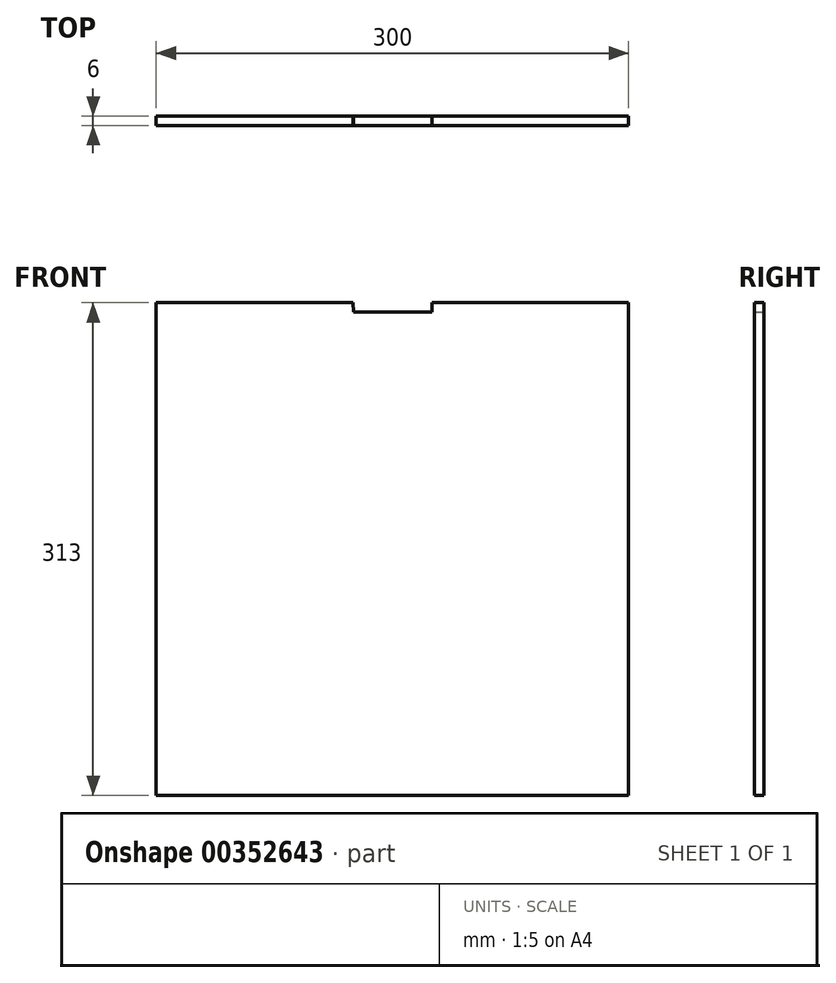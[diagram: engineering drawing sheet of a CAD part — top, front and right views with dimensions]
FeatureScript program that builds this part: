
annotation { "Feature Type Name" : "Feature", "Feature Type Description" : "" }
export const myFeature = defineFeature(function(context is Context, id is Id, definition is map)
    precondition{}
    {
        {
            var Q0;
            Q0=qCreatedBy(makeId("Front.planeOp"),FACE);
            var sketch = newSketch(context, id + "F0", { "sketchPlane" : qUnion([Q0])});
            skLineSegment(sketch, "E0", {"start": v(-46.12, 181.72) * mm, "end": v(-46.03, 175.72) * mm});
            skLineSegment(sketch, "E1", {"start": v(3.97, 175.72) * mm, "end": v(3.88, 181.72) * mm});
            skLineSegment(sketch, "E2.MirrorCS", {"start": v(-46.12, 181.72) * mm, "end": v(-171.12, 181.72) * mm});
            skLineSegment(sketch, "E3.MirrorCS", {"start": v(3.88, 181.72) * mm, "end": v(128.88, 181.72) * mm});
            skLineSegment(sketch, "E4", {"start": v(-46.03, 175.72) * mm, "end": v(3.97, 175.72) * mm});
            skLineSegment(sketch, "E5", {"start": v(-171.12, -131.28) * mm, "end": v(128.88, -131.28) * mm});
            skLineSegment(sketch, "E6", {"start": v(-171.12, 181.72) * mm, "end": v(-171.12, -131.28) * mm});
            skLineSegment(sketch, "E7", {"start": v(128.88, 181.72) * mm, "end": v(128.88, -131.28) * mm});
            skSolve(sketch);
        }
        {
            var Q0;
            Q0=qSketchRegion(id+"F0",true);
            extrude(context, id + "F1", {"entities" : qUnion([Q0]), "depth" : 6 * mm});
        }
    });
